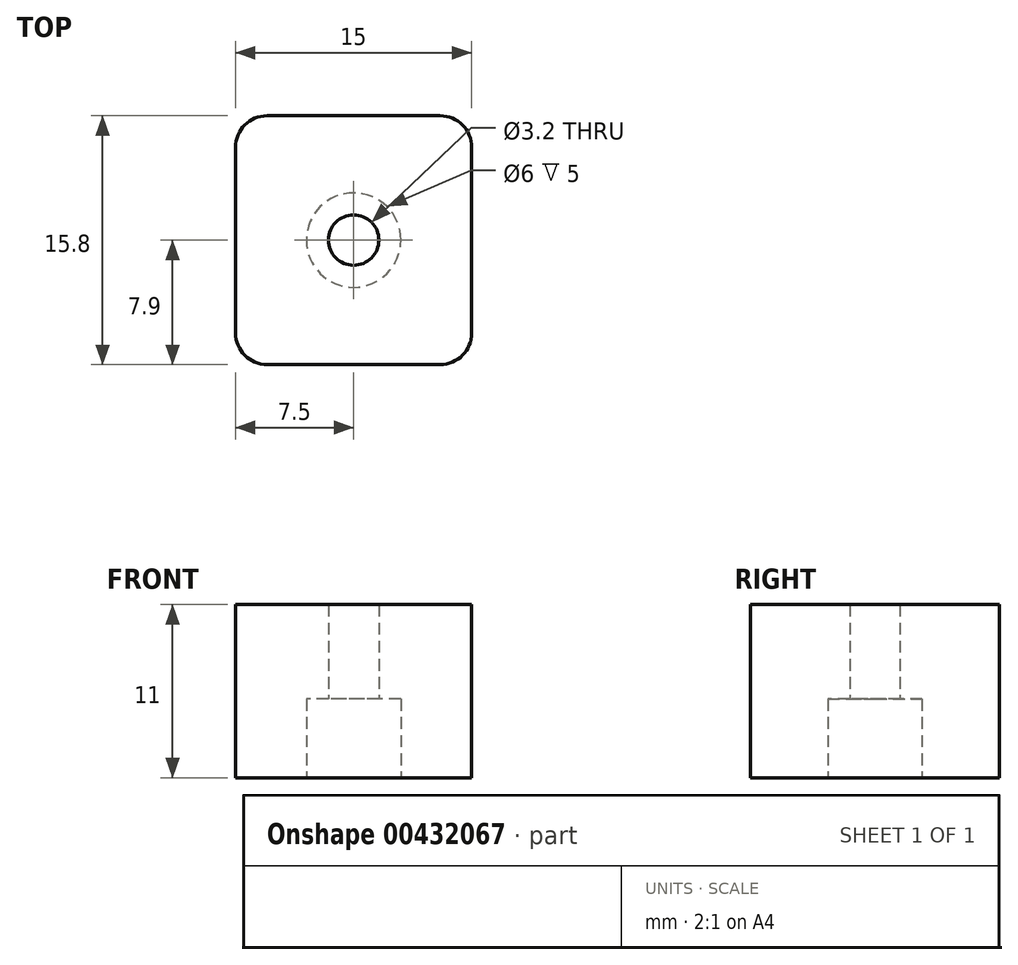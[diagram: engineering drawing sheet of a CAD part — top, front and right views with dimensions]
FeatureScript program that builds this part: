
annotation { "Feature Type Name" : "Feature", "Feature Type Description" : "" }
export const myFeature = defineFeature(function(context is Context, id is Id, definition is map)
    precondition{}
    {
        {
            var Q0;
            Q0=qCreatedBy(makeId("Top.planeOp"),FACE);
            var sketch = newSketch(context, id + "F0", { "sketchPlane" : qUnion([Q0])});
            skLineSegment(sketch, "E0.bottom", {"start": v(7.5, -7.9) * mm, "end": v(-7.5, -7.9) * mm});
            skLineSegment(sketch, "E0.top", {"start": v(7.5, 7.9) * mm, "end": v(-7.5, 7.9) * mm});
            skLineSegment(sketch, "E0.left", {"start": v(7.5, -7.9) * mm, "end": v(7.5, 7.9) * mm});
            skLineSegment(sketch, "E0.right", {"start": v(-7.5, -7.9) * mm, "end": v(-7.5, 7.9) * mm});
            skPoint(sketch, "E0.middle", {"position": v(0, 0) * mm});
            skCircle(sketch, "E1", {"center": v(0, 0) * mm, "radius": 1.6 * mm});
            skCircle(sketch, "E2", {"center": v(0, 0) * mm, "radius": 3 * mm});
            skSolve(sketch);
        }
        {
            var Q0;
            Q0=makeQuery(id+"F0.imprint","IMPRINT",FACE,{"disambiguationData":[TD([[makeQuery(id+"F0.imprint","IMPRINT",EDGE,{"derivedFrom":sQuery(id+"F0.wireOp",EDGE,"E0.bottom")}),-1.0]])]});
            var Q1;
            Q1=makeQuery(id+"F0.imprint","IMPRINT",FACE,{"disambiguationData":[TD([[makeQuery(id+"F0.imprint","IMPRINT",EDGE,{"derivedFrom":sQuery(id+"F0.wireOp",EDGE,"E1")}),-1.0]])]});
            extrude(context, id + "F1", {"entities" : qUnion([Q0, Q1]), "depth" : 11 * mm});
        }
        {
            var Q0;
            Q0=makeQuery(id+"F0.imprint","IMPRINT",FACE,{"disambiguationData":[TD([[makeQuery(id+"F0.imprint","IMPRINT",EDGE,{"derivedFrom":sQuery(id+"F0.wireOp",EDGE,"E1")}),-1.0]])]});
            extrude(context, id + "F2", {"entities" : qUnion([Q0]), "operationType" : NewBodyOperationType.REMOVE, "depth" : 5 * mm});
        }
        {
            var Q0;
            Q0=makeQuery(id+"F1.opExtrude","SWEPT_EDGE",EDGE,{"disambiguationData":[OSD([sQuery(id+"F0.wireOp",EDGE,"E0.top"),sQuery(id+"F0.wireOp",EDGE,"E0.right")])]});
            var Q1;
            Q1=makeQuery(id+"F1.opExtrude","SWEPT_EDGE",EDGE,{"disambiguationData":[OSD([sQuery(id+"F0.wireOp",EDGE,"E0.bottom"),sQuery(id+"F0.wireOp",EDGE,"E0.right")])]});
            var Q2;
            Q2=makeQuery(id+"F1.opExtrude","SWEPT_EDGE",EDGE,{"disambiguationData":[OSD([sQuery(id+"F0.wireOp",EDGE,"E0.bottom"),sQuery(id+"F0.wireOp",EDGE,"E0.left")])]});
            var Q3;
            Q3=makeQuery(id+"F1.opExtrude","SWEPT_EDGE",EDGE,{"disambiguationData":[OSD([sQuery(id+"F0.wireOp",EDGE,"E0.top"),sQuery(id+"F0.wireOp",EDGE,"E0.left")])]});
            fillet(context, id + "F3", {"entities" : qUnion([Q0, Q1, Q2, Q3]), "radius" : 2 * mm, "tangentPropagation" : true, "allowEdgeOverflow" : false});
        }
    });
